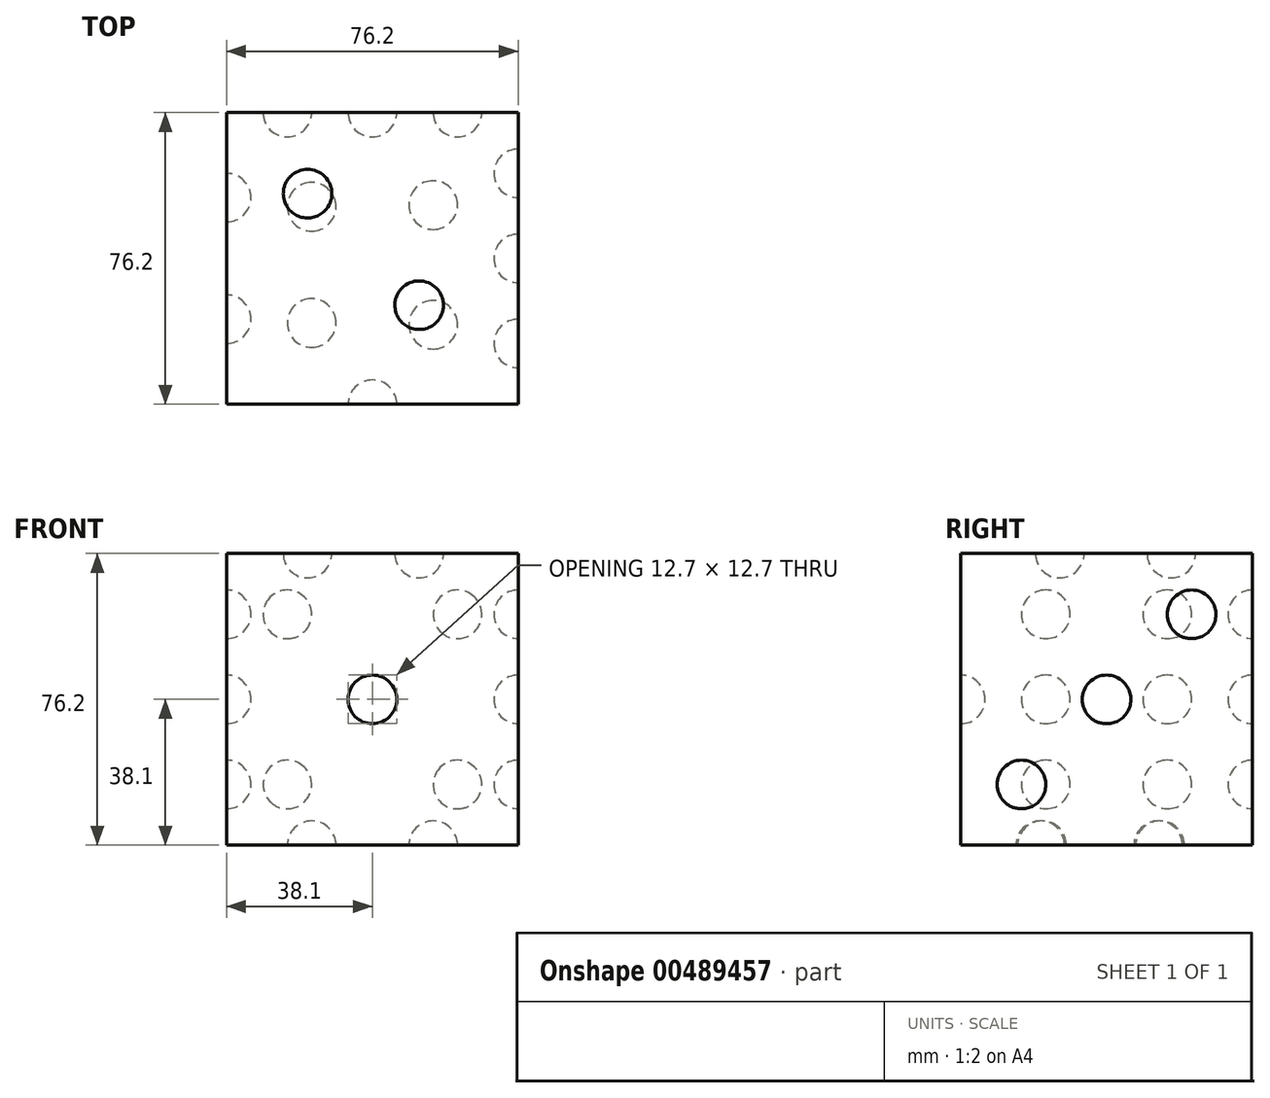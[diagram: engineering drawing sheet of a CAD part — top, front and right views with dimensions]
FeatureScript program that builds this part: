
annotation { "Feature Type Name" : "Feature", "Feature Type Description" : "" }
export const myFeature = defineFeature(function(context is Context, id is Id, definition is map)
    precondition{}
    {
        {
            var Q0;
            Q0=qCreatedBy(makeId("Front.planeOp"),FACE);
            var sketch = newSketch(context, id + "F0", { "sketchPlane" : qUnion([Q0])});
            skLineSegment(sketch, "E0", {"start": v(0, 0) * mm, "end": v(76.2, 0) * mm});
            skLineSegment(sketch, "E1", {"start": v(76.2, 76.2) * mm, "end": v(76.2, 0) * mm});
            skLineSegment(sketch, "E2", {"start": v(76.2, 76.2) * mm, "end": v(0, 76.2) * mm});
            skLineSegment(sketch, "E3", {"start": v(0, 76.2) * mm, "end": v(0, 0) * mm});
            skSolve(sketch);
        }
        {
            var Q0;
            Q0=makeQuery(id+"F0.imprint","IMPRINT",FACE,{"disambiguationData":[TD([[makeQuery(id+"F0.imprint","IMPRINT",EDGE,{"derivedFrom":sQuery(id+"F0.wireOp",EDGE,"E0")}),1.0]])]});
            extrude(context, id + "F1", {"entities" : qUnion([Q0]), "depth" : 76.2 * mm});
        }
        {
            var Q0;
            Q0=makeQuery(id+"F1.opExtrude","CAP_FACE",FACE,{"disambiguationData":[OSD([sQuery(id+"F0.wireOp",EDGE,"E0"),sQuery(id+"F0.wireOp",EDGE,"E1"),sQuery(id+"F0.wireOp",EDGE,"E2"),sQuery(id+"F0.wireOp",EDGE,"E3")])],"isStart":false});
            var sketch = newSketch(context, id + "F2", { "sketchPlane" : qUnion([Q0])});
            skArc(sketch, "E4", {"start": v(38.1, 31.75) * mm, "mid": v(44.45, 38.1) * mm, "end": v(38.1, 44.45) * mm});
            skPoint(sketch, "E4.centerSnap0", {"position": v(76.2, 38.1) * mm});
            skPoint(sketch, "E4.centerSnap1", {"position": v(38.1, 76.2) * mm});
            skLineSegment(sketch, "E5", {"start": v(38.1, 0) * mm, "end": v(38.1, 76.2) * mm});
            skSolve(sketch);
        }
        {
            var Q0;
            {var subQ0=sQuery(id+"F2.wireOp",EDGE,"E4");Q0=makeQuery(id+"F2.imprint","IMPRINT",FACE,{"disambiguationData":[TD([[makeQuery(id+"F2.imprint","IMPRINT",EDGE,{"derivedFrom":subQ0}),1.0]])]});}
            var Q1;
            Q1=sQuery(id+"F2.wireOp",EDGE,"E5");
            revolve(context, id + "F3", {"operationType" : NewBodyOperationType.REMOVE, "entities" : qUnion([Q0]), "axis" : qUnion([Q1]), "revolveType" : RevolveType.FULL, "oppositeDirection" : true});
        }
        {
            var Q0;
            Q0=makeQuery(id+"F1.opExtrude","SWEPT_FACE",FACE,{"disambiguationData":[OSD([sQuery(id+"F0.wireOp",EDGE,"E1")])]});
            var sketch = newSketch(context, id + "F4", { "sketchPlane" : qUnion([Q0])});
            skLineSegment(sketch, "E6", {"start": v(0, 76.2) * mm, "end": v(-76.2, 0) * mm});
            skArc(sketch, "E7", {"start": v(-42.6, 33.6) * mm, "mid": v(-33.6, 33.6) * mm, "end": v(-33.6, 42.6) * mm});
            skArc(sketch, "E8", {"start": v(-64.82, 11.38) * mm, "mid": v(-55.83, 11.38) * mm, "end": v(-55.83, 20.37) * mm});
            skArc(sketch, "E9", {"start": v(-20.37, 55.83) * mm, "mid": v(-11.38, 55.83) * mm, "end": v(-11.38, 64.82) * mm});
            skSolve(sketch);
        }
        {
            var Q0;
            {var subQ0=sQuery(id+"F4.wireOp",EDGE,"E7");Q0=makeQuery(id+"F4.imprint","IMPRINT",FACE,{"disambiguationData":[TD([[makeQuery(id+"F4.imprint","IMPRINT",EDGE,{"derivedFrom":subQ0}),1.0]])]});}
            var Q1;
            {var subQ0=sQuery(id+"F4.wireOp",EDGE,"E9");Q1=makeQuery(id+"F4.imprint","IMPRINT",FACE,{"disambiguationData":[TD([[makeQuery(id+"F4.imprint","IMPRINT",EDGE,{"derivedFrom":subQ0}),1.0]])]});}
            var Q2;
            {var subQ0=sQuery(id+"F4.wireOp",EDGE,"E8");Q2=makeQuery(id+"F4.imprint","IMPRINT",FACE,{"disambiguationData":[TD([[makeQuery(id+"F4.imprint","IMPRINT",EDGE,{"derivedFrom":subQ0}),1.0]])]});}
            var Q3;
            Q3=sQuery(id+"F4.wireOp",EDGE,"E6");
            revolve(context, id + "F5", {"operationType" : NewBodyOperationType.REMOVE, "entities" : qUnion([Q0, Q1, Q2]), "axis" : qUnion([Q3]), "revolveType" : RevolveType.FULL, "oppositeDirection" : true});
        }
        {
            var Q0;
            Q0=makeQuery(id+"F1.opExtrude","CAP_FACE",FACE,{"disambiguationData":[OSD([sQuery(id+"F0.wireOp",EDGE,"E0"),sQuery(id+"F0.wireOp",EDGE,"E1"),sQuery(id+"F0.wireOp",EDGE,"E2"),sQuery(id+"F0.wireOp",EDGE,"E3")])],"isStart":true});
            var sketch = newSketch(context, id + "F6", { "sketchPlane" : qUnion([Q0])});
            skLineSegment(sketch, "E10", {"start": v(-76.2, 76.2) * mm, "end": v(0, 0) * mm});
            skLineSegment(sketch, "E11", {"start": v(0, 76.2) * mm, "end": v(-76.2, 0) * mm});
            skArc(sketch, "E12", {"start": v(-33.6, 33.6) * mm, "mid": v(-33.6, 42.6) * mm, "end": v(-42.6, 42.6) * mm});
            skArc(sketch, "E13", {"start": v(-20.37, 55.83) * mm, "mid": v(-11.38, 55.83) * mm, "end": v(-11.38, 64.82) * mm});
            skArc(sketch, "E14", {"start": v(-11.38, 11.38) * mm, "mid": v(-11.38, 20.37) * mm, "end": v(-20.37, 20.37) * mm});
            skArc(sketch, "E15", {"start": v(-64.82, 11.38) * mm, "mid": v(-55.83, 11.38) * mm, "end": v(-55.83, 20.37) * mm});
            skArc(sketch, "E16", {"start": v(-55.83, 55.83) * mm, "mid": v(-55.83, 64.82) * mm, "end": v(-64.82, 64.82) * mm});
            skSolve(sketch);
        }
        {
            var Q0;
            {var subQ0=sQuery(id+"F6.wireOp",EDGE,"E16");Q0=makeQuery(id+"F6.imprint","IMPRINT",FACE,{"disambiguationData":[TD([[makeQuery(id+"F6.imprint","IMPRINT",EDGE,{"derivedFrom":subQ0}),1.0]])]});}
            var Q1;
            {var subQ0=sQuery(id+"F6.wireOp",EDGE,"E12");var subQ1=sQuery(id+"F6.wireOp",EDGE,"E10");var subQ2=makeQuery(id+"F6.imprint","INTERSECT",VERTEX,{"disambiguationData":[OD(1.0)],"derivedFrom":[subQ1,subQ0]});Q1=makeQuery(id+"F6.imprint","IMPRINT",FACE,{"disambiguationData":[TD([[makeQuery(id+"F6.imprint","IMPRINT",EDGE,{"disambiguationData":[TD([[subQ2,-1.0]])],"derivedFrom":subQ1}),1.0]])]});}
            var Q2;
            {var subQ0=sQuery(id+"F6.wireOp",EDGE,"E12");var subQ1=sQuery(id+"F6.wireOp",EDGE,"E10");var subQ2=makeQuery(id+"F6.imprint","INTERSECT",VERTEX,{"disambiguationData":[OD(0.0)],"derivedFrom":[subQ1,subQ0]});Q2=makeQuery(id+"F6.imprint","IMPRINT",FACE,{"disambiguationData":[TD([[makeQuery(id+"F6.imprint","IMPRINT",EDGE,{"disambiguationData":[TD([[subQ2,1.0]])],"derivedFrom":subQ1}),1.0]])]});}
            var Q3;
            {var subQ0=sQuery(id+"F6.wireOp",EDGE,"E14");Q3=makeQuery(id+"F6.imprint","IMPRINT",FACE,{"disambiguationData":[TD([[makeQuery(id+"F6.imprint","IMPRINT",EDGE,{"derivedFrom":subQ0}),1.0]])]});}
            var Q4;
            Q4=sQuery(id+"F6.wireOp",EDGE,"E10");
            revolve(context, id + "F7", {"operationType" : NewBodyOperationType.REMOVE, "entities" : qUnion([Q0, Q1, Q2, Q3]), "axis" : qUnion([Q4]), "revolveType" : RevolveType.FULL});
        }
        {
            var Q0;
            Q0=makeQuery(id+"F1.opExtrude","CAP_FACE",FACE,{"disambiguationData":[OSD([sQuery(id+"F0.wireOp",EDGE,"E0"),sQuery(id+"F0.wireOp",EDGE,"E1"),sQuery(id+"F0.wireOp",EDGE,"E2"),sQuery(id+"F0.wireOp",EDGE,"E3")])],"isStart":true});
            var sketch = newSketch(context, id + "F8", { "sketchPlane" : qUnion([Q0])});
            skLineSegment(sketch, "E17", {"start": v(0, 76.2) * mm, "end": v(-76.2, 0) * mm});
            skArc(sketch, "E18", {"start": v(-20.37, 55.83) * mm, "mid": v(-11.38, 55.83) * mm, "end": v(-11.38, 64.82) * mm});
            skArc(sketch, "E19", {"start": v(-64.82, 11.38) * mm, "mid": v(-55.83, 11.38) * mm, "end": v(-55.83, 20.37) * mm});
            skArc(sketch, "E20", {"start": v(-42.6, 33.6) * mm, "mid": v(-33.6, 33.6) * mm, "end": v(-33.6, 42.6) * mm});
            skPoint(sketch, "E21.orphan", {"position": v(-76.2, 76.2) * mm});
            skPoint(sketch, "E22.end.orphan", {"position": v(0, 0) * mm});
            skSolve(sketch);
        }
        {
            var Q0;
            {var subQ0=sQuery(id+"F8.wireOp",EDGE,"E20");Q0=makeQuery(id+"F8.imprint","IMPRINT",FACE,{"disambiguationData":[TD([[makeQuery(id+"F8.imprint","IMPRINT",EDGE,{"derivedFrom":subQ0}),1.0]])]});}
            var Q1;
            {var subQ0=sQuery(id+"F8.wireOp",EDGE,"E18");Q1=makeQuery(id+"F8.imprint","IMPRINT",FACE,{"disambiguationData":[TD([[makeQuery(id+"F8.imprint","IMPRINT",EDGE,{"derivedFrom":subQ0}),1.0]])]});}
            var Q2;
            {var subQ0=sQuery(id+"F8.wireOp",EDGE,"E19");Q2=makeQuery(id+"F8.imprint","IMPRINT",FACE,{"disambiguationData":[TD([[makeQuery(id+"F8.imprint","IMPRINT",EDGE,{"derivedFrom":subQ0}),1.0]])]});}
            var Q3;
            Q3=sQuery(id+"F8.wireOp",EDGE,"E17");
            revolve(context, id + "F9", {"operationType" : NewBodyOperationType.REMOVE, "entities" : qUnion([Q0, Q1, Q2]), "axis" : qUnion([Q3]), "revolveType" : RevolveType.FULL, "oppositeDirection" : true});
        }
        {
            var Q0;
            Q0=makeQuery(id+"F1.opExtrude","SWEPT_FACE",FACE,{"disambiguationData":[OSD([sQuery(id+"F0.wireOp",EDGE,"E3")])]});
            var sketch = newSketch(context, id + "F10", { "sketchPlane" : qUnion([Q0])});
            skLineSegment(sketch, "E23", {"start": v(22.22, 76.2) * mm, "end": v(22.23, 0) * mm});
            skLineSegment(sketch, "E24", {"start": v(53.98, 76.2) * mm, "end": v(53.98, 0) * mm});
            skArc(sketch, "E25", {"start": v(22.23, 31.75) * mm, "mid": v(28.58, 38.1) * mm, "end": v(22.23, 44.45) * mm});
            skArc(sketch, "E26", {"start": v(53.98, 31.75) * mm, "mid": v(60.33, 38.1) * mm, "end": v(53.98, 44.45) * mm});
            skArc(sketch, "E27", {"start": v(53.98, 53.98) * mm, "mid": v(60.33, 60.33) * mm, "end": v(53.98, 66.67) * mm});
            skArc(sketch, "E28", {"start": v(22.22, 53.98) * mm, "mid": v(28.58, 60.32) * mm, "end": v(22.23, 66.67) * mm});
            skArc(sketch, "E29", {"start": v(22.23, 9.52) * mm, "mid": v(28.58, 15.87) * mm, "end": v(22.23, 22.23) * mm});
            skArc(sketch, "E30", {"start": v(53.98, 9.52) * mm, "mid": v(60.33, 15.88) * mm, "end": v(53.98, 22.23) * mm});
            skSolve(sketch);
        }
        {
            var Q0;
            {var subQ0=sQuery(id+"F10.wireOp",EDGE,"E28");Q0=makeQuery(id+"F10.imprint","IMPRINT",FACE,{"disambiguationData":[TD([[makeQuery(id+"F10.imprint","IMPRINT",EDGE,{"derivedFrom":subQ0}),1.0]])]});}
            var Q1;
            {var subQ0=sQuery(id+"F10.wireOp",EDGE,"E25");Q1=makeQuery(id+"F10.imprint","IMPRINT",FACE,{"disambiguationData":[TD([[makeQuery(id+"F10.imprint","IMPRINT",EDGE,{"derivedFrom":subQ0}),1.0]])]});}
            var Q2;
            {var subQ0=sQuery(id+"F10.wireOp",EDGE,"E29");Q2=makeQuery(id+"F10.imprint","IMPRINT",FACE,{"disambiguationData":[TD([[makeQuery(id+"F10.imprint","IMPRINT",EDGE,{"derivedFrom":subQ0}),1.0]])]});}
            var Q3;
            Q3=sQuery(id+"F10.wireOp",EDGE,"E23");
            revolve(context, id + "F11", {"operationType" : NewBodyOperationType.REMOVE, "entities" : qUnion([Q0, Q1, Q2]), "axis" : qUnion([Q3]), "revolveType" : RevolveType.FULL, "oppositeDirection" : true});
        }
        {
            var Q0;
            Q0=makeQuery(id+"F1.opExtrude","SWEPT_FACE",FACE,{"disambiguationData":[OSD([sQuery(id+"F0.wireOp",EDGE,"E3")])]});
            var sketch = newSketch(context, id + "F12", { "sketchPlane" : qUnion([Q0])});
            skLineSegment(sketch, "E31", {"start": v(53.98, 76.2) * mm, "end": v(53.98, 0) * mm});
            skArc(sketch, "E32", {"start": v(53.98, 31.75) * mm, "mid": v(60.33, 38.1) * mm, "end": v(53.98, 44.45) * mm});
            skArc(sketch, "E33", {"start": v(53.98, 53.98) * mm, "mid": v(60.33, 60.33) * mm, "end": v(53.98, 66.67) * mm});
            skArc(sketch, "E34", {"start": v(53.98, 9.52) * mm, "mid": v(60.33, 15.88) * mm, "end": v(53.98, 22.23) * mm});
            skSolve(sketch);
        }
        {
            var Q0;
            {var subQ0=sQuery(id+"F12.wireOp",EDGE,"E32");Q0=makeQuery(id+"F12.imprint","IMPRINT",FACE,{"disambiguationData":[TD([[makeQuery(id+"F12.imprint","IMPRINT",EDGE,{"derivedFrom":subQ0}),1.0]])]});}
            var Q1;
            {var subQ0=sQuery(id+"F12.wireOp",EDGE,"E33");Q1=makeQuery(id+"F12.imprint","IMPRINT",FACE,{"disambiguationData":[TD([[makeQuery(id+"F12.imprint","IMPRINT",EDGE,{"derivedFrom":subQ0}),1.0]])]});}
            var Q2;
            {var subQ0=sQuery(id+"F12.wireOp",EDGE,"E34");Q2=makeQuery(id+"F12.imprint","IMPRINT",FACE,{"disambiguationData":[TD([[makeQuery(id+"F12.imprint","IMPRINT",EDGE,{"derivedFrom":subQ0}),1.0]])]});}
            var Q3;
            Q3=sQuery(id+"F12.wireOp",EDGE,"E31");
            revolve(context, id + "F13", {"operationType" : NewBodyOperationType.REMOVE, "entities" : qUnion([Q0, Q1, Q2]), "axis" : qUnion([Q3]), "revolveType" : RevolveType.FULL});
        }
        {
            var Q0;
            Q0=makeQuery(id+"F1.opExtrude","SWEPT_FACE",FACE,{"disambiguationData":[OSD([sQuery(id+"F0.wireOp",EDGE,"E2")])]});
            var sketch = newSketch(context, id + "F14", { "sketchPlane" : qUnion([Q0])});
            skLineSegment(sketch, "E35", {"start": v(0, 0) * mm, "end": v(76.2, -76.2) * mm});
            skArc(sketch, "E36", {"start": v(25.66, -25.66) * mm, "mid": v(25.66, -16.68) * mm, "end": v(16.68, -16.68) * mm});
            skArc(sketch, "E37", {"start": v(54.8, -54.8) * mm, "mid": v(54.8, -45.82) * mm, "end": v(45.82, -45.82) * mm});
            skSolve(sketch);
        }
        {
            var Q0;
            {var subQ0=sQuery(id+"F14.wireOp",EDGE,"E36");Q0=makeQuery(id+"F14.imprint","IMPRINT",FACE,{"disambiguationData":[TD([[makeQuery(id+"F14.imprint","IMPRINT",EDGE,{"derivedFrom":subQ0}),1.0]])]});}
            var Q1;
            {var subQ0=sQuery(id+"F14.wireOp",EDGE,"E37");Q1=makeQuery(id+"F14.imprint","IMPRINT",FACE,{"disambiguationData":[TD([[makeQuery(id+"F14.imprint","IMPRINT",EDGE,{"derivedFrom":subQ0}),1.0]])]});}
            var Q2;
            Q2=sQuery(id+"F14.wireOp",EDGE,"E35");
            revolve(context, id + "F15", {"operationType" : NewBodyOperationType.REMOVE, "entities" : qUnion([Q0, Q1]), "axis" : qUnion([Q2]), "revolveType" : RevolveType.FULL, "oppositeDirection" : true});
        }
        {
            var Q0;
            Q0=makeQuery(id+"F1.opExtrude","SWEPT_FACE",FACE,{"disambiguationData":[OSD([sQuery(id+"F0.wireOp",EDGE,"E0")])]});
            var sketch = newSketch(context, id + "F16", { "sketchPlane" : qUnion([Q0])});
            skLineSegment(sketch, "E38", {"start": v(22.22, 76.2) * mm, "end": v(22.23, 0) * mm});
            skLineSegment(sketch, "E39", {"start": v(53.98, 76.2) * mm, "end": v(53.98, 0) * mm});
            skArc(sketch, "E40", {"start": v(22.23, 48.62) * mm, "mid": v(28.58, 54.97) * mm, "end": v(22.23, 61.32) * mm});
            skArc(sketch, "E41", {"start": v(22.23, 18.25) * mm, "mid": v(28.58, 24.6) * mm, "end": v(22.23, 30.95) * mm});
            skArc(sketch, "E42", {"start": v(53.98, 17.8) * mm, "mid": v(60.33, 24.16) * mm, "end": v(53.98, 30.5) * mm});
            skArc(sketch, "E43", {"start": v(53.98, 49.06) * mm, "mid": v(60.33, 55.4) * mm, "end": v(53.98, 61.76) * mm});
            skSolve(sketch);
        }
        {
            var Q0;
            {var subQ0=sQuery(id+"F16.wireOp",EDGE,"E40");Q0=makeQuery(id+"F16.imprint","IMPRINT",FACE,{"disambiguationData":[TD([[makeQuery(id+"F16.imprint","IMPRINT",EDGE,{"derivedFrom":subQ0}),1.0]])]});}
            var Q1;
            {var subQ0=sQuery(id+"F16.wireOp",EDGE,"E41");Q1=makeQuery(id+"F16.imprint","IMPRINT",FACE,{"disambiguationData":[TD([[makeQuery(id+"F16.imprint","IMPRINT",EDGE,{"derivedFrom":subQ0}),1.0]])]});}
            var Q2;
            Q2=sQuery(id+"F16.wireOp",EDGE,"E38");
            revolve(context, id + "F17", {"operationType" : NewBodyOperationType.REMOVE, "entities" : qUnion([Q0, Q1]), "axis" : qUnion([Q2]), "revolveType" : RevolveType.FULL, "oppositeDirection" : true});
        }
        {
            var Q0;
            {var subQ0=sQuery(id+"F16.wireOp",EDGE,"E43");Q0=makeQuery(id+"F16.imprint","IMPRINT",FACE,{"disambiguationData":[TD([[makeQuery(id+"F16.imprint","IMPRINT",EDGE,{"derivedFrom":subQ0}),1.0]])]});}
            var Q1;
            {var subQ0=sQuery(id+"F16.wireOp",EDGE,"E42");Q1=makeQuery(id+"F16.imprint","IMPRINT",FACE,{"disambiguationData":[TD([[makeQuery(id+"F16.imprint","IMPRINT",EDGE,{"derivedFrom":subQ0}),1.0]])]});}
            var Q2;
            Q2=sQuery(id+"F16.wireOp",EDGE,"E39");
            revolve(context, id + "F18", {"operationType" : NewBodyOperationType.REMOVE, "entities" : qUnion([Q0, Q1]), "axis" : qUnion([Q2]), "revolveType" : RevolveType.FULL, "oppositeDirection" : true});
        }
    });
